# Revit family: QF_EVEREST_EGSDH2
name_source: partatom
category: Specialty Equipment
revit_build: Autodesk Revit 2015 (Build: 20160512_0715(x64)
units: mm (PartAtom-declared; Revit-internal decimal feet)

## types (2) — shared parameters
Apparent Power = 0 VA
BTUH = 3435.0 Btu/h
Conn Conduit = Yes
Conn Plug = NEMA 5-15P
Cycle = 60 Hz
Depth = 803 mm  [stored 2.63451 ft]
Description = UPRIGHT REACH–IN REFRIGERATOR
FL Amps = 8 A
Foodservice Equipment Identifier = Yes
HP = 1/2
Height = 2010 mm  [stored 6.59449 ft]
Identify Quantity as Lot = Yes
Length = 740 mm  [stored 2.42782 ft]
Manufacturer = EVEREST
Max Overcurrent Protection = 0 A
Min Ckt Ampacity = 0 A
Model = EGSDH2
Number of Poles = 1
Phase = 1
Refrigerant Volume = 0.00 kip
Volts = 115 V
Watts = 871 W
zero-valued in all types: Elec Conn Connection Height, Elec Conn RI Height

## per-type parameters (varying)
| type | Electrical Remarks | Refrigerant Type | Weight in Pounds |
| QF_EVEREST_EGSDH2 | COMES IN R-404A AND R290 REFRIGERANT VARIANTS. | R-404A / R290 | 356 |
| QF_EVEREST_EGSH2 |  | R-404A | 342 |

note: [stored X ft] marks values corroborated as IEEE doubles in the binary element streams (Revit-internal decimal feet)

## geometry (parser evidence)
native form markers: Sweep x2
no freeform markers — native parametric forms only
